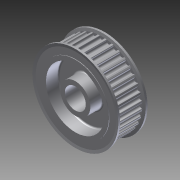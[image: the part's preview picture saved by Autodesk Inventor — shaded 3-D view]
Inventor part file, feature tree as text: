
AUTODESK INVENTOR PART (.ipt)
format: ipt  version: 2014 SP1 (Build 180222100, 222)  size: 1,051,648 bytes
history: native  units: in
note: dims shown in document units (in); Inventor stores cm internally (conversion verified against a paired STEP export)
features: mirror x1, other x1, extrude x1, imported_body x1, sketch x1
ambient origin geometry x8: Origin, YZ Plane, XZ Plane, XY Plane, X Axis, Y Axis, Z Axis, Center Point
bodies: Body1 (feature_tree)
feature tree (5):
  mirror  "Mirror1"
  other  "217-3232-STEP1"
  extrude  "Extrusion1"  [1 undecoded]
  imported_body  "Base1"
  sketch  "Sketch1"  dims[d0=39.3701in d1=0.0in]
note: 1 required parameter value undecoded (feature->parameter linkage not recoverable at this tier; creation-order binding heuristic only, values carry confidence <= 0.55)
